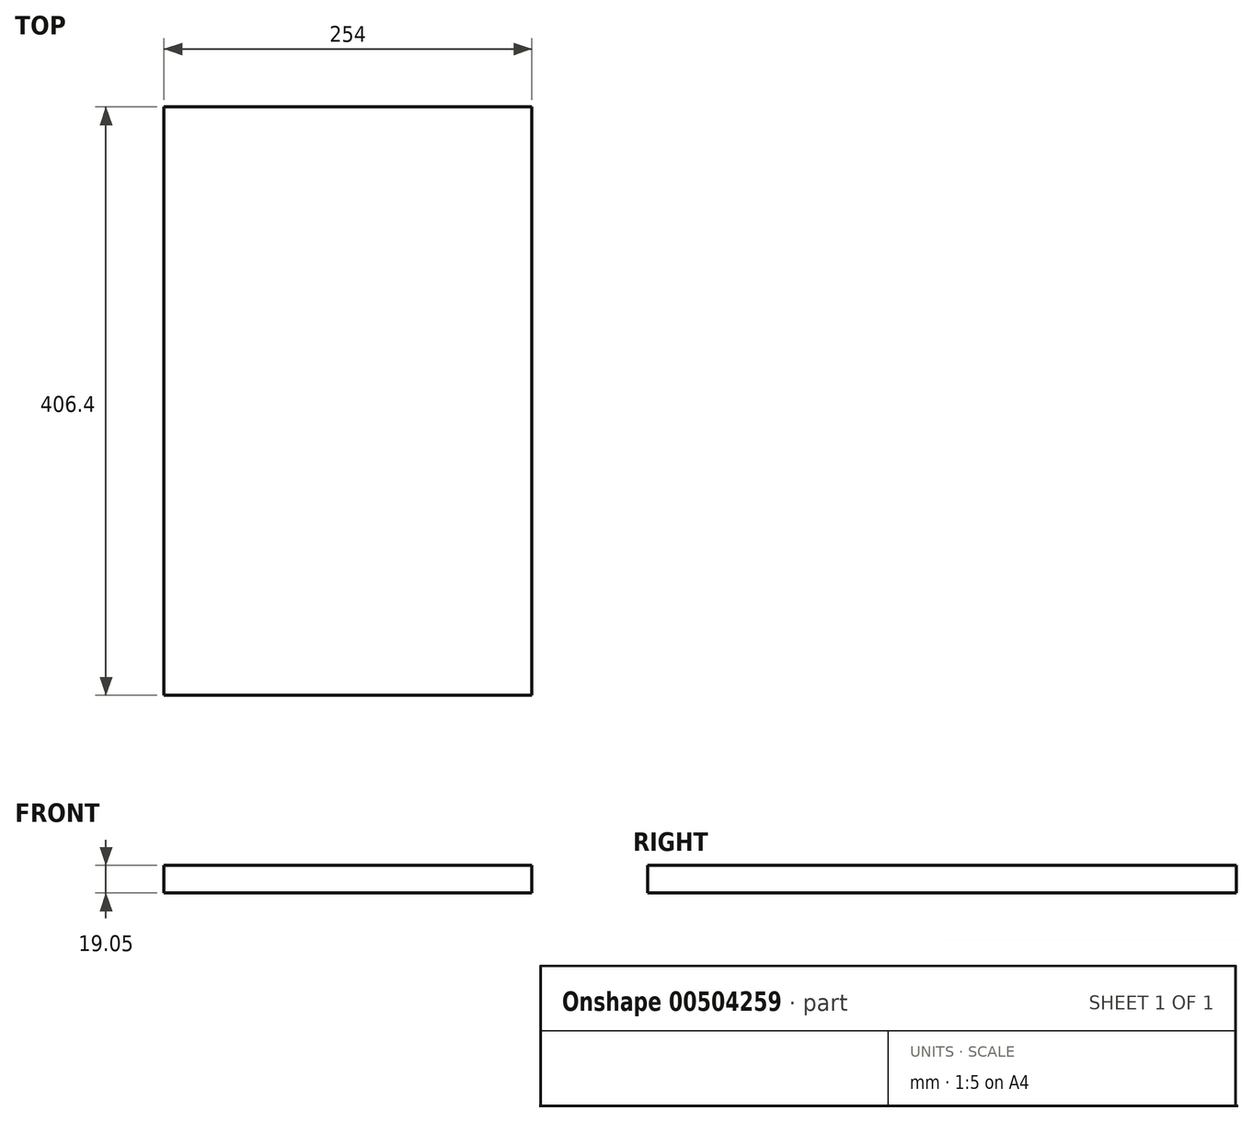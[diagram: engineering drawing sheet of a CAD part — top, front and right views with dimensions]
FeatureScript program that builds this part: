
annotation { "Feature Type Name" : "Feature", "Feature Type Description" : "" }
export const myFeature = defineFeature(function(context is Context, id is Id, definition is map)
    precondition{}
    {
        {
            var Q0;
            Q0=qCreatedBy(makeId("Top.planeOp"),FACE);
            var sketch = newSketch(context, id + "F0", { "sketchPlane" : qUnion([Q0])});
            skLineSegment(sketch, "E0.bottom", {"start": v(127, -203.2) * mm, "end": v(-127, -203.2) * mm});
            skLineSegment(sketch, "E0.top", {"start": v(127, 203.2) * mm, "end": v(-127, 203.2) * mm});
            skLineSegment(sketch, "E0.left", {"start": v(127, -203.2) * mm, "end": v(127, 203.2) * mm});
            skLineSegment(sketch, "E0.right", {"start": v(-127, -203.2) * mm, "end": v(-127, 203.2) * mm});
            skPoint(sketch, "E0.middle", {"position": v(0, 0) * mm});
            skSolve(sketch);
        }
        {
            var Q0;
            Q0=makeQuery(id+"F0.imprint","IMPRINT",FACE,{"disambiguationData":[TD([[makeQuery(id+"F0.imprint","IMPRINT",EDGE,{"derivedFrom":sQuery(id+"F0.wireOp",EDGE,"E0.bottom")}),-1.0]])]});
            extrude(context, id + "F1", {"entities" : qUnion([Q0]), "depth" : 19.05 * mm});
        }
    });
